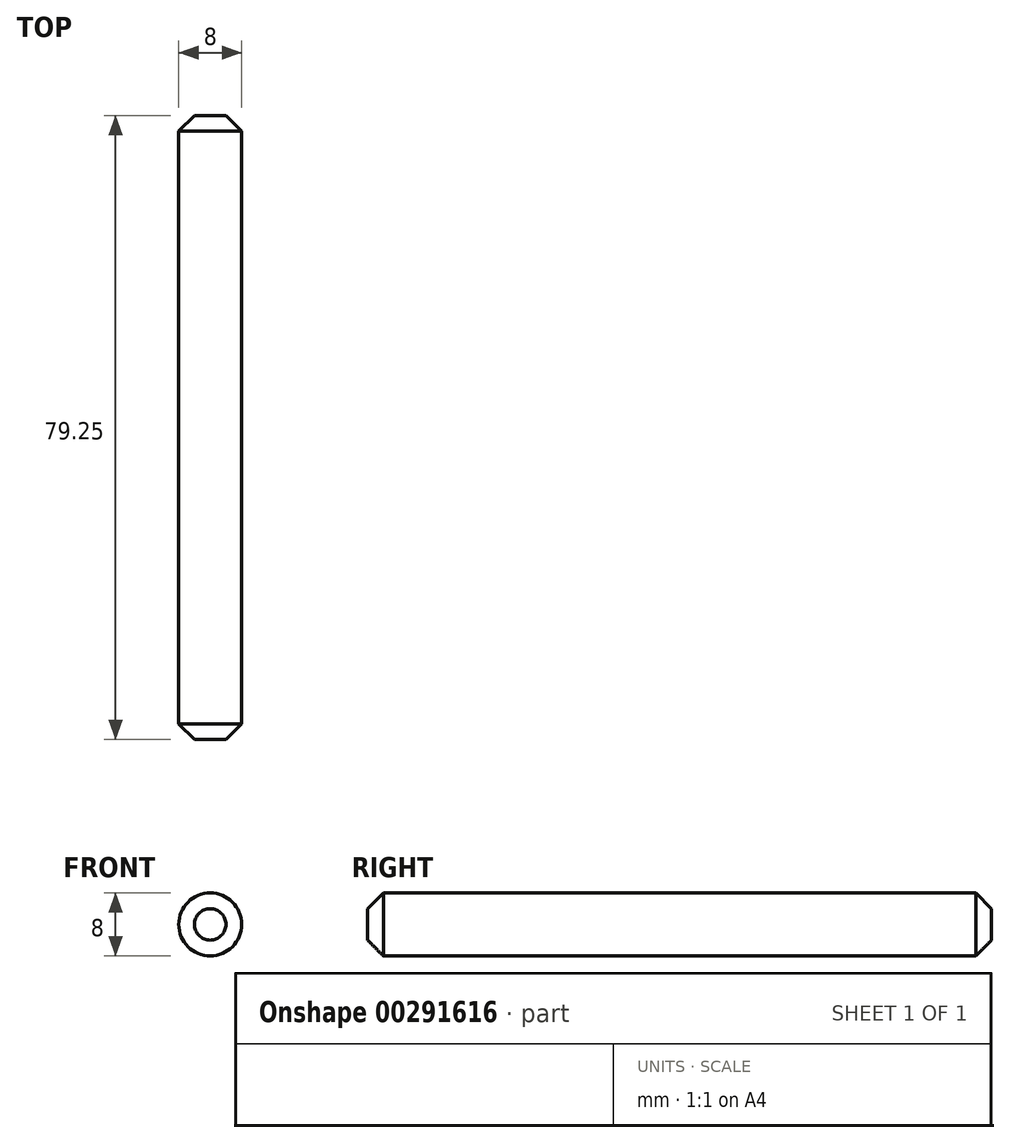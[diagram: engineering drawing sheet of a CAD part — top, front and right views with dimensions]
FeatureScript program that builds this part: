
annotation { "Feature Type Name" : "Feature", "Feature Type Description" : "" }
export const myFeature = defineFeature(function(context is Context, id is Id, definition is map)
    precondition{}
    {
        {
            var Q0;
            Q0=qCreatedBy(makeId("Front.planeOp"),FACE);
            var sketch = newSketch(context, id + "F0", { "sketchPlane" : qUnion([Q0])});
            skCircle(sketch, "E0", {"center": v(0, 0) * mm, "radius": 4 * mm});
            skSolve(sketch);
        }
        {
            var Q0;
            Q0=makeQuery(id+"F0.imprint","IMPRINT",FACE,{"disambiguationData":[TD([[makeQuery(id+"F0.imprint","IMPRINT",EDGE,{"derivedFrom":sQuery(id+"F0.wireOp",EDGE,"E0")}),1.0]])]});
            var Q1;
            Q1=sQuery(id+"F0.wireOp",EDGE,"E0");
            extrude(context, id + "F1", {"entities" : qUnion([Q0]), "surfaceEntities" : qUnion([Q1]), "oppositeDirection" : true, "depth" : 79.25 * mm});
        }
        {
            var Q0;
            Q0=makeQuery(id+"F1.opExtrude","CAP_EDGE",EDGE,{"disambiguationData":[OSD([sQuery(id+"F0.wireOp",EDGE,"E0")])],"isStart":true});
            var Q1;
            Q1=makeQuery(id+"F1.opExtrude","CAP_EDGE",EDGE,{"disambiguationData":[OSD([sQuery(id+"F0.wireOp",EDGE,"E0")])],"isStart":false});
            chamfer(context, id + "F2", {"entities" : qUnion([Q0, Q1]), "width" : 2 * mm, "tangentPropagation" : true});
        }
    });
